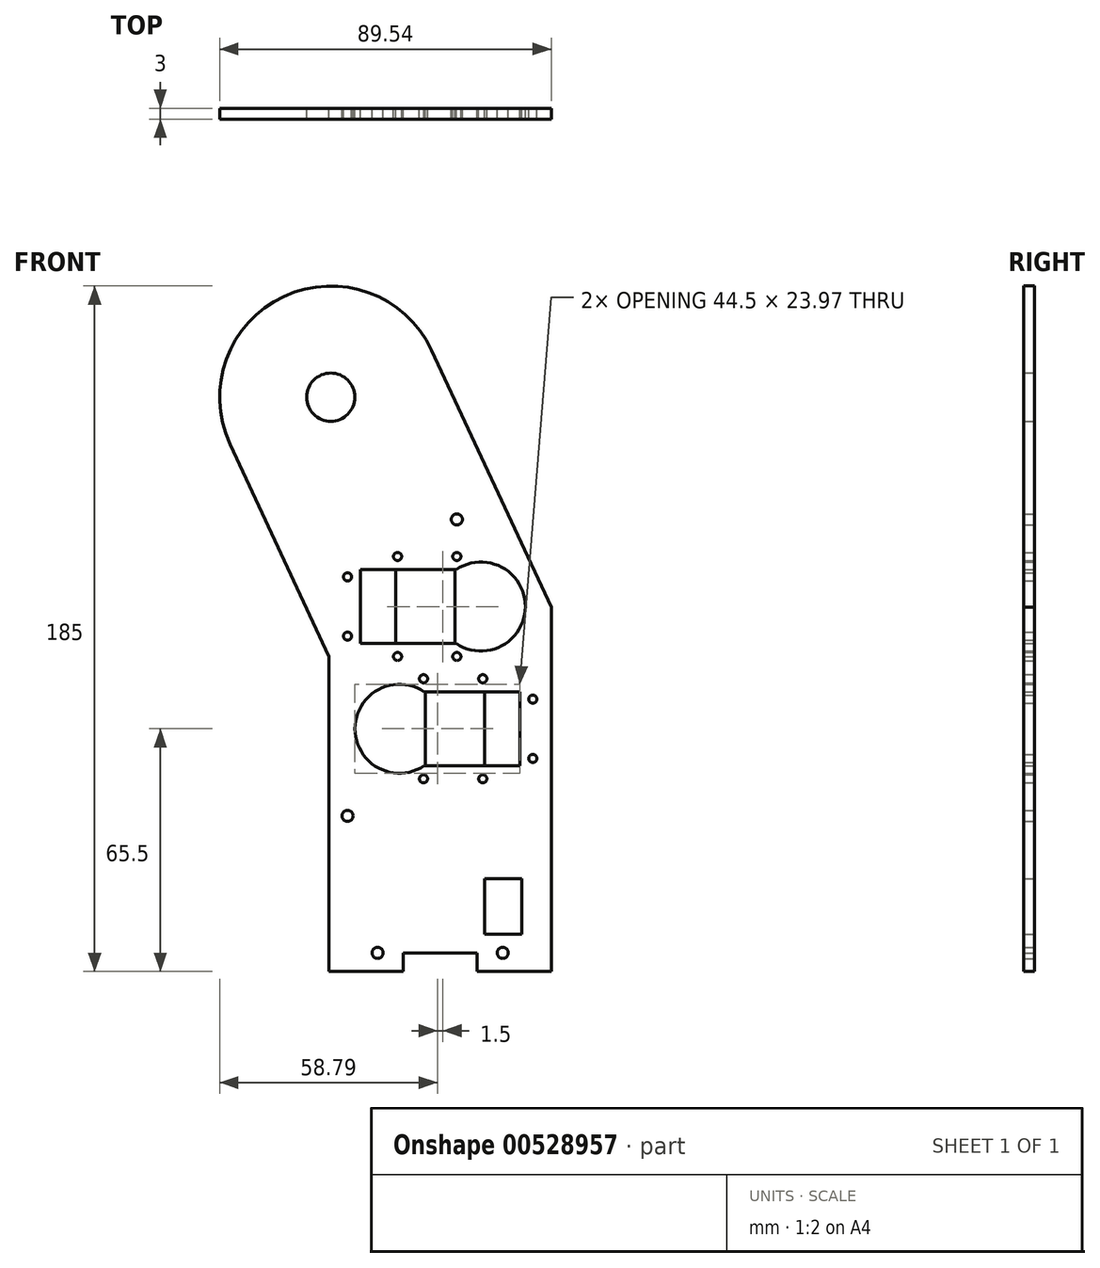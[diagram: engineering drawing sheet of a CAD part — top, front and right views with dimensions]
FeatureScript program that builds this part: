
annotation { "Feature Type Name" : "Feature", "Feature Type Description" : "" }
export const myFeature = defineFeature(function(context is Context, id is Id, definition is map)
    precondition{}
    {
        {
            var Q0;
            Q0=qCreatedBy(makeId("Front.planeOp"),FACE);
            var sketch = newSketch(context, id + "F0", { "sketchPlane" : qUnion([Q0])});
            skArc(sketch, "E0", {"start": v(-27.19, -12.68) * mm, "mid": v(-12.68, 27.19) * mm, "end": v(27.19, 12.68) * mm});
            skCircle(sketch, "E1", {"center": v(0, 0) * mm, "radius": 6.5 * mm});
            skLineSegment(sketch, "E2", {"start": v(-0.46, -150) * mm, "end": v(59.54, -150) * mm, "construction": true});
            skLineSegment(sketch, "E3", {"start": v(-0.46, -150) * mm, "end": v(-0.46, -70) * mm});
            skLineSegment(sketch, "E4", {"start": v(-0.46, -70) * mm, "end": v(-27.19, -12.68) * mm});
            skLineSegment(sketch, "E5", {"start": v(27.19, 12.68) * mm, "end": v(59.54, -56.7) * mm});
            skLineSegment(sketch, "E6", {"start": v(59.54, -56.7) * mm, "end": v(59.54, -150) * mm});
            skLineSegment(sketch, "E7", {"start": v(-0.46, -150) * mm, "end": v(-0.46, -155) * mm});
            skLineSegment(sketch, "E8", {"start": v(-0.46, -155) * mm, "end": v(19.54, -155) * mm});
            skLineSegment(sketch, "E9", {"start": v(19.54, -155) * mm, "end": v(19.54, -150) * mm});
            skLineSegment(sketch, "E10", {"start": v(39.54, -150) * mm, "end": v(39.54, -155) * mm});
            skLineSegment(sketch, "E11", {"start": v(39.54, -155) * mm, "end": v(59.54, -155) * mm});
            skLineSegment(sketch, "E12", {"start": v(59.54, -155) * mm, "end": v(59.54, -150) * mm});
            skLineSegment(sketch, "E13", {"start": v(19.54, -150) * mm, "end": v(39.54, -150) * mm});
            skCircle(sketch, "E14", {"center": v(18.54, -89.5) * mm, "radius": 12 * mm});
            skPoint(sketch, "E15", {"position": v(25.04, -76) * mm});
            skPoint(sketch, "E16", {"position": v(41.04, -76) * mm});
            skPoint(sketch, "E17", {"position": v(25.04, -103) * mm});
            skPoint(sketch, "E18", {"position": v(41.04, -103) * mm});
            skPoint(sketch, "E19", {"position": v(54.54, -97.5) * mm});
            skPoint(sketch, "E20", {"position": v(54.54, -81.5) * mm});
            skLineSegment(sketch, "E21", {"start": v(18.54, -89.5) * mm, "end": v(51.04, -89.5) * mm, "construction": true});
            skLineSegment(sketch, "E22", {"start": v(25.17, -79.5) * mm, "end": v(51.04, -79.5) * mm});
            skLineSegment(sketch, "E23", {"start": v(51.04, -79.5) * mm, "end": v(51.04, -99.5) * mm});
            skLineSegment(sketch, "E24", {"start": v(51.04, -99.5) * mm, "end": v(25.17, -99.5) * mm});
            skCircle(sketch, "E25", {"center": v(25.04, -76) * mm, "radius": 1.1 * mm});
            skCircle(sketch, "E26", {"center": v(41.04, -76) * mm, "radius": 1.1 * mm});
            skCircle(sketch, "E27", {"center": v(54.54, -81.5) * mm, "radius": 1.1 * mm});
            skCircle(sketch, "E28", {"center": v(54.54, -97.5) * mm, "radius": 1.1 * mm});
            skCircle(sketch, "E29", {"center": v(41.04, -103) * mm, "radius": 1.1 * mm});
            skCircle(sketch, "E30", {"center": v(25.04, -103) * mm, "radius": 1.1 * mm});
            skLineSegment(sketch, "E31.bottom", {"start": v(17.54, -46.5) * mm, "end": v(33.54, -46.5) * mm});
            skLineSegment(sketch, "E31.top", {"start": v(17.54, -66.5) * mm, "end": v(33.54, -66.5) * mm});
            skLineSegment(sketch, "E31.left", {"start": v(17.54, -46.5) * mm, "end": v(17.54, -66.5) * mm});
            skLineSegment(sketch, "E31.right", {"start": v(33.54, -46.5) * mm, "end": v(33.54, -66.5) * mm});
            skLineSegment(sketch, "E32", {"start": v(33.54, -56.5) * mm, "end": v(17.54, -56.5) * mm, "construction": true});
            skPoint(sketch, "E33", {"position": v(18.04, -43) * mm});
            skPoint(sketch, "E34", {"position": v(34.04, -43) * mm});
            skPoint(sketch, "E35", {"position": v(34.04, -70) * mm});
            skPoint(sketch, "E36", {"position": v(18.04, -70) * mm});
            skPoint(sketch, "E37", {"position": v(4.54, -48.5) * mm});
            skPoint(sketch, "E38", {"position": v(4.54, -64.5) * mm});
            skCircle(sketch, "E39", {"center": v(4.54, -48.5) * mm, "radius": 1.1 * mm});
            skCircle(sketch, "E40", {"center": v(4.54, -64.5) * mm, "radius": 1.1 * mm});
            skCircle(sketch, "E41", {"center": v(18.04, -70) * mm, "radius": 1.1 * mm});
            skCircle(sketch, "E42", {"center": v(34.04, -70) * mm, "radius": 1.1 * mm});
            skCircle(sketch, "E43", {"center": v(34.04, -43) * mm, "radius": 1.1 * mm});
            skCircle(sketch, "E44", {"center": v(18.04, -43) * mm, "radius": 1.1 * mm});
            skCircle(sketch, "E45", {"center": v(12.64, -150) * mm, "radius": 1.5 * mm});
            skCircle(sketch, "E46", {"center": v(46.44, -150) * mm, "radius": 1.5 * mm});
            skLineSegment(sketch, "E47", {"start": v(29.54, -150) * mm, "end": v(29.54, -144.6) * mm, "construction": true});
            skCircle(sketch, "E48", {"center": v(34.04, -33) * mm, "radius": 1.5 * mm});
            skCircle(sketch, "E49", {"center": v(4.54, -113) * mm, "radius": 1.5 * mm});
            skLineSegment(sketch, "E50.bottom", {"start": v(41.54, -130) * mm, "end": v(51.54, -130) * mm});
            skLineSegment(sketch, "E50.top", {"start": v(41.54, -145) * mm, "end": v(51.54, -145) * mm});
            skLineSegment(sketch, "E50.left", {"start": v(41.54, -130) * mm, "end": v(41.54, -145) * mm});
            skLineSegment(sketch, "E50.right", {"start": v(51.54, -130) * mm, "end": v(51.54, -145) * mm});
            skSolve(sketch);
        }
        {
            var Q0;
            Q0=qCreatedBy(makeId("Front.planeOp"),FACE);
            var sketch = newSketch(context, id + "F1", { "sketchPlane" : qUnion([Q0])});
            skArc(sketch, "E51", {"start": v(-27.19, -12.68) * mm, "mid": v(-12.68, 27.19) * mm, "end": v(27.19, 12.68) * mm});
            skCircle(sketch, "E52", {"center": v(0, 0) * mm, "radius": 6.5 * mm});
            skLineSegment(sketch, "E53", {"start": v(-0.46, -150) * mm, "end": v(59.54, -150) * mm, "construction": true});
            skLineSegment(sketch, "E54", {"start": v(-0.46, -150) * mm, "end": v(-0.46, -70) * mm});
            skLineSegment(sketch, "E55", {"start": v(-0.46, -70) * mm, "end": v(-27.19, -12.68) * mm});
            skLineSegment(sketch, "E56", {"start": v(27.19, 12.68) * mm, "end": v(59.54, -56.7) * mm});
            skLineSegment(sketch, "E57", {"start": v(59.54, -56.7) * mm, "end": v(59.54, -150) * mm});
            skLineSegment(sketch, "E58", {"start": v(-0.46, -150) * mm, "end": v(-0.46, -155) * mm});
            skLineSegment(sketch, "E59", {"start": v(-0.46, -155) * mm, "end": v(19.54, -155) * mm});
            skLineSegment(sketch, "E60", {"start": v(19.54, -155) * mm, "end": v(19.54, -150) * mm});
            skLineSegment(sketch, "E61", {"start": v(39.54, -150) * mm, "end": v(39.54, -155) * mm});
            skLineSegment(sketch, "E62", {"start": v(39.54, -155) * mm, "end": v(59.54, -155) * mm});
            skLineSegment(sketch, "E63", {"start": v(59.54, -155) * mm, "end": v(59.54, -150) * mm});
            skLineSegment(sketch, "E64", {"start": v(19.54, -150) * mm, "end": v(39.54, -150) * mm});
            skLineSegment(sketch, "E65.bottom", {"start": v(25.54, -79.5) * mm, "end": v(41.54, -79.5) * mm});
            skLineSegment(sketch, "E65.top", {"start": v(25.54, -99.5) * mm, "end": v(41.54, -99.5) * mm});
            skLineSegment(sketch, "E65.left", {"start": v(25.54, -79.5) * mm, "end": v(25.54, -99.5) * mm});
            skLineSegment(sketch, "E65.right", {"start": v(41.54, -79.5) * mm, "end": v(41.54, -99.5) * mm});
            skCircle(sketch, "E66", {"center": v(40.54, -56.5) * mm, "radius": 12 * mm});
            skLineSegment(sketch, "E67", {"start": v(40.54, -56.5) * mm, "end": v(8.04, -56.5) * mm, "construction": true});
            skLineSegment(sketch, "E68", {"start": v(8.04, -66.5) * mm, "end": v(8.04, -46.5) * mm});
            skLineSegment(sketch, "E69", {"start": v(8.04, -46.5) * mm, "end": v(33.9, -46.5) * mm});
            skLineSegment(sketch, "E70", {"start": v(8.04, -66.5) * mm, "end": v(33.9, -66.5) * mm});
            skPoint(sketch, "E71", {"position": v(18.04, -43) * mm});
            skPoint(sketch, "E72", {"position": v(34.04, -43) * mm});
            skPoint(sketch, "E73", {"position": v(18.04, -70) * mm});
            skPoint(sketch, "E74", {"position": v(34.04, -70) * mm});
            skPoint(sketch, "E75", {"position": v(4.54, -48.5) * mm});
            skPoint(sketch, "E76", {"position": v(4.54, -64.5) * mm});
            skCircle(sketch, "E77", {"center": v(18.04, -43) * mm, "radius": 1.1 * mm});
            skCircle(sketch, "E78", {"center": v(34.04, -43) * mm, "radius": 1.1 * mm});
            skCircle(sketch, "E79", {"center": v(34.04, -70) * mm, "radius": 1.1 * mm});
            skCircle(sketch, "E80", {"center": v(18.04, -70) * mm, "radius": 1.1 * mm});
            skCircle(sketch, "E81", {"center": v(4.54, -64.5) * mm, "radius": 1.1 * mm});
            skCircle(sketch, "E82", {"center": v(4.54, -48.5) * mm, "radius": 1.1 * mm});
            skLineSegment(sketch, "E83", {"start": v(25.54, -89.5) * mm, "end": v(41.54, -89.5) * mm, "construction": true});
            skPoint(sketch, "E84", {"position": v(54.54, -81.5) * mm});
            skPoint(sketch, "E85", {"position": v(54.54, -97.5) * mm});
            skPoint(sketch, "E86", {"position": v(25.04, -103) * mm});
            skPoint(sketch, "E87", {"position": v(41.04, -103) * mm});
            skPoint(sketch, "E88", {"position": v(41.04, -76) * mm});
            skPoint(sketch, "E89", {"position": v(25.04, -76) * mm});
            skCircle(sketch, "E90", {"center": v(25.04, -76) * mm, "radius": 1.1 * mm});
            skCircle(sketch, "E91", {"center": v(41.04, -76) * mm, "radius": 1.1 * mm});
            skCircle(sketch, "E92", {"center": v(54.54, -81.5) * mm, "radius": 1.1 * mm});
            skCircle(sketch, "E93", {"center": v(54.54, -97.5) * mm, "radius": 1.1 * mm});
            skCircle(sketch, "E94", {"center": v(41.04, -103) * mm, "radius": 1.1 * mm});
            skCircle(sketch, "E95", {"center": v(25.04, -103) * mm, "radius": 1.1 * mm});
            skLineSegment(sketch, "E96", {"start": v(29.54, -150) * mm, "end": v(29.54, -142.65) * mm, "construction": true});
            skCircle(sketch, "E97", {"center": v(46.44, -150) * mm, "radius": 1.5 * mm});
            skCircle(sketch, "E98", {"center": v(12.64, -150) * mm, "radius": 1.5 * mm});
            skCircle(sketch, "E99", {"center": v(34.04, -33) * mm, "radius": 1.5 * mm});
            skCircle(sketch, "E100", {"center": v(4.54, -113) * mm, "radius": 1.5 * mm});
            skLineSegment(sketch, "E101.bottom", {"start": v(41.54, -130) * mm, "end": v(51.54, -130) * mm});
            skLineSegment(sketch, "E101.top", {"start": v(41.54, -145) * mm, "end": v(51.54, -145) * mm});
            skLineSegment(sketch, "E101.left", {"start": v(41.54, -130) * mm, "end": v(41.54, -145) * mm});
            skLineSegment(sketch, "E101.right", {"start": v(51.54, -130) * mm, "end": v(51.54, -145) * mm});
            skSolve(sketch);
        }
        {
            var Q0;
            Q0 = qSketchRegion(id + "F0", true);
            extrude(context, id + "F2", {"entities" : qUnion([Q0]), "depth" : 3 * mm, "offsetDistance" : 25 * mm});
        }
        {
            var Q0;
            Q0 = qSketchRegion(id + "F1", true);
            extrude(context, id + "F3", {"entities" : qUnion([Q0]), "depth" : 3 * mm, "offsetDistance" : 25 * mm});
        }
    });
